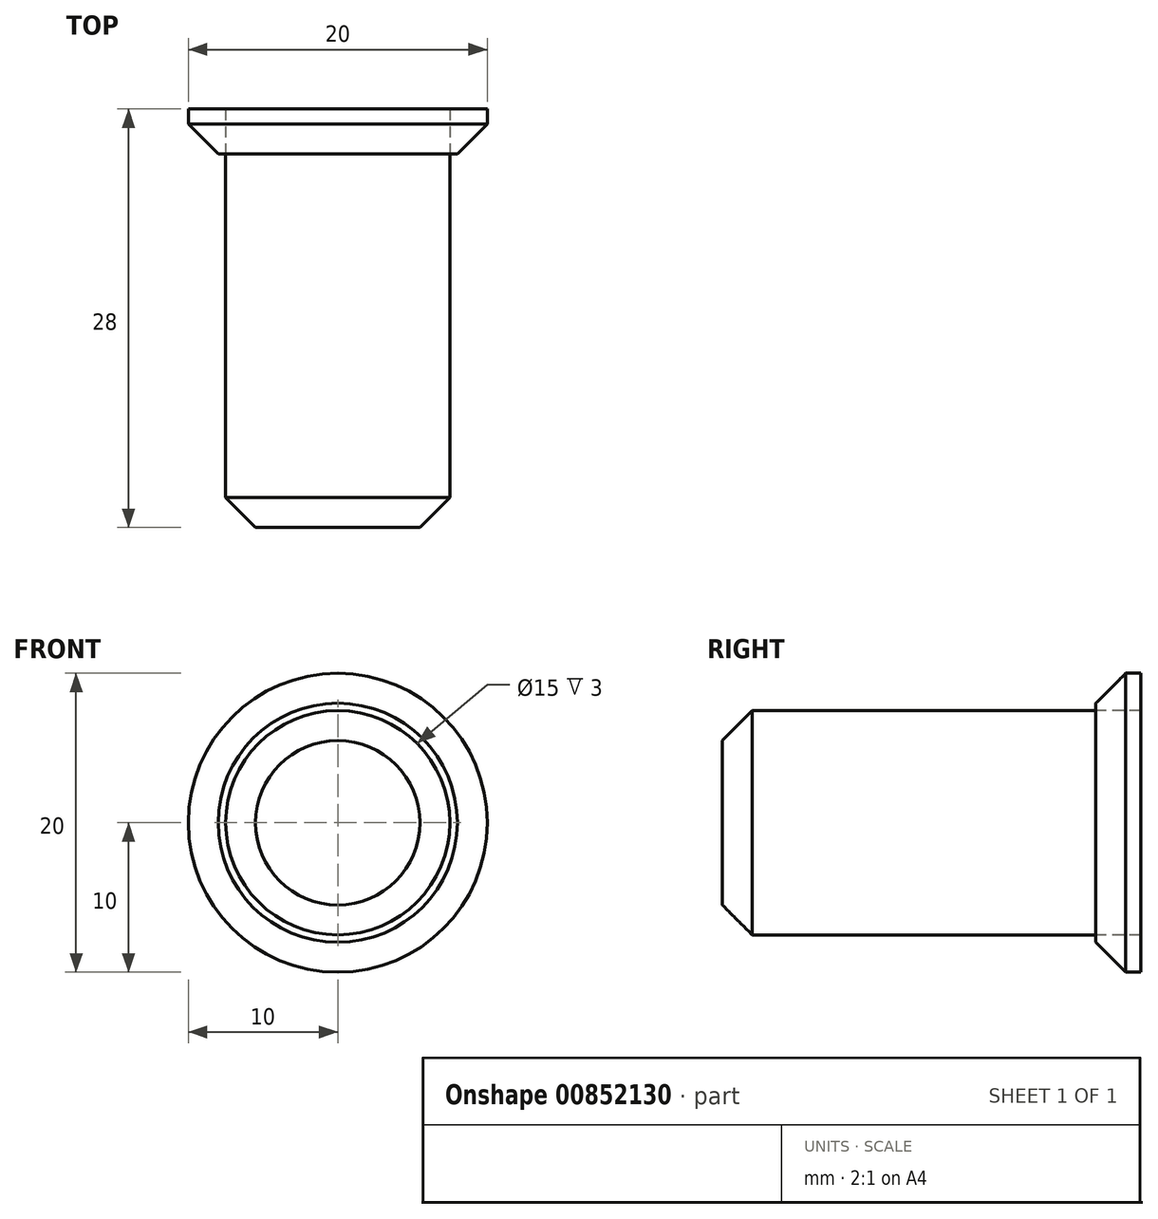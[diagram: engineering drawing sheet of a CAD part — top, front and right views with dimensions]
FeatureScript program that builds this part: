
annotation { "Feature Type Name" : "Feature", "Feature Type Description" : "" }
export const myFeature = defineFeature(function(context is Context, id is Id, definition is map)
    precondition{}
    {
        {
            var Q0;
            Q0=qCreatedBy(makeId("Front.planeOp"),FACE);
            var sketch = newSketch(context, id + "F0", { "sketchPlane" : qUnion([Q0])});
            skCircle(sketch, "E0", {"center": v(0, 0) * mm, "radius": 7.5 * mm});
            skSolve(sketch);
        }
        {
            var Q0;
            Q0=makeQuery(id+"F0.imprint","IMPRINT",FACE,{"disambiguationData":[TD([[makeQuery(id+"F0.imprint","IMPRINT",EDGE,{"derivedFrom":sQuery(id+"F0.wireOp",EDGE,"E0")}),1.0]])]});
            extrude(context, id + "F1", {"entities" : qUnion([Q0]), "depth" : 25 * mm, "offsetDistance" : 25 * mm});
        }
        {
            var Q0;
            Q0=makeQuery(id+"F1.opExtrude","CAP_EDGE",EDGE,{"disambiguationData":[OSD([sQuery(id+"F0.wireOp",EDGE,"E0")])],"isStart":false});
            chamfer(context, id + "F2", {"entities" : qUnion([Q0]), "width" : 2 * mm, "tangentPropagation" : true});
        }
        {
            var Q0;
            Q0=makeQuery(id+"F1.opExtrude","CAP_FACE",FACE,{"disambiguationData":[OSD([sQuery(id+"F0.wireOp",EDGE,"E0")])],"isStart":true});
            var sketch = newSketch(context, id + "F3", { "sketchPlane" : qUnion([Q0])});
            skCircle(sketch, "E1", {"center": v(0, 0) * mm, "radius": 10 * mm});
            skSolve(sketch);
        }
        {
            var Q0;
            Q0=makeQuery(id+"F3.imprint","IMPRINT",FACE,{"disambiguationData":[TD([[makeQuery(id+"F3.imprint","IMPRINT",EDGE,{"derivedFrom":sQuery(id+"F3.wireOp",EDGE,"E1")}),1.0]])]});
            extrude(context, id + "F4", {"entities" : qUnion([Q0]), "depth" : 3 * mm, "offsetDistance" : 25 * mm});
        }
        {
            var Q0;
            Q0=makeQuery(id+"F4.opExtrude","CAP_EDGE",EDGE,{"disambiguationData":[OSD([sQuery(id+"F3.wireOp",EDGE,"E1")])],"isStart":true});
            chamfer(context, id + "F5", {"entities" : qUnion([Q0]), "width" : 2 * mm, "tangentPropagation" : true});
        }
    });
